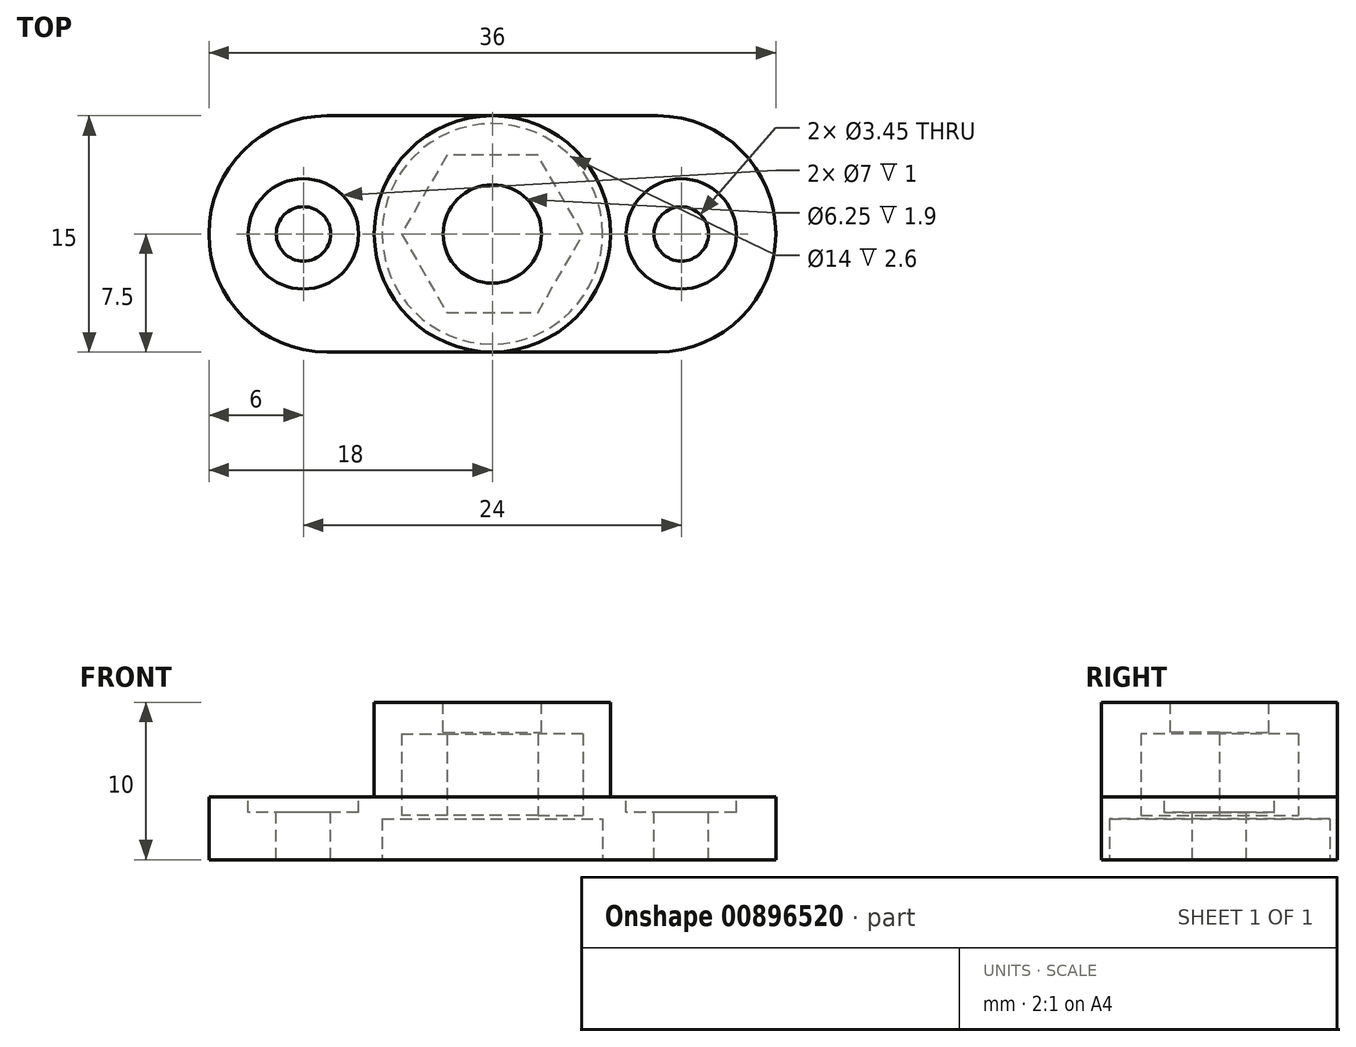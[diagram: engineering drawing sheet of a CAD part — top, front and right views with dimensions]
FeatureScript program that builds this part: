
annotation { "Feature Type Name" : "Feature", "Feature Type Description" : "" }
export const myFeature = defineFeature(function(context is Context, id is Id, definition is map)
    precondition{}
    {
        {
            var Q0;
            Q0=qCreatedBy(makeId("Top.planeOp"),FACE);
            var sketch = newSketch(context, id + "F0", { "sketchPlane" : qUnion([Q0])});
            skLineSegment(sketch, "E0.bottom", {"start": v(18, 7.5) * mm, "end": v(-18, 7.5) * mm});
            skLineSegment(sketch, "E0.top", {"start": v(18, -7.5) * mm, "end": v(-18, -7.5) * mm});
            skLineSegment(sketch, "E0.left", {"start": v(18, 7.5) * mm, "end": v(18, -7.5) * mm});
            skLineSegment(sketch, "E0.right", {"start": v(-18, 7.5) * mm, "end": v(-18, -7.5) * mm});
            skPoint(sketch, "E0.middle", {"position": v(0, 0) * mm});
            skSolve(sketch);
        }
        {
            var Q0;
            Q0 = qSketchRegion(id + "F0", true);
            extrude(context, id + "F1", {"entities" : qUnion([Q0]), "depth" : 4 * mm, "offsetDistance" : 25 * mm});
        }
        {
            var Q0;
            Q0=makeQuery(id+"F1.opExtrude","CAP_FACE",FACE,{"disambiguationData":[OSD([sQuery(id+"F0.wireOp",EDGE,"E0.bottom"),sQuery(id+"F0.wireOp",EDGE,"E0.top"),sQuery(id+"F0.wireOp",EDGE,"E0.left"),sQuery(id+"F0.wireOp",EDGE,"E0.right")])],"isStart":false});
            var sketch = newSketch(context, id + "F2", { "sketchPlane" : qUnion([Q0])});
            skCircle(sketch, "E1", {"center": v(0, 0) * mm, "radius": 7.5 * mm});
            skSolve(sketch);
        }
        {
            var Q0;
            Q0 = qSketchRegion(id + "F2", true);
            extrude(context, id + "F3", {"entities" : qUnion([Q0]), "operationType" : NewBodyOperationType.ADD, "depth" : 6 * mm, "offsetDistance" : 25 * mm});
        }
        {
            var Q0;
            Q0=makeQuery(id+"F1.opExtrude","SWEPT_EDGE",EDGE,{"disambiguationData":[OSD([sQuery(id+"F0.wireOp",EDGE,"E0.top"),sQuery(id+"F0.wireOp",EDGE,"E0.right")])]});
            var Q1;
            Q1=makeQuery(id+"F1.opExtrude","SWEPT_EDGE",EDGE,{"disambiguationData":[OSD([sQuery(id+"F0.wireOp",EDGE,"E0.bottom"),sQuery(id+"F0.wireOp",EDGE,"E0.right")])]});
            var Q2;
            Q2=makeQuery(id+"F1.opExtrude","SWEPT_EDGE",EDGE,{"disambiguationData":[OSD([sQuery(id+"F0.wireOp",EDGE,"E0.top"),sQuery(id+"F0.wireOp",EDGE,"E0.left")])]});
            var Q3;
            Q3=makeQuery(id+"F1.opExtrude","SWEPT_EDGE",EDGE,{"disambiguationData":[OSD([sQuery(id+"F0.wireOp",EDGE,"E0.bottom"),sQuery(id+"F0.wireOp",EDGE,"E0.left")])]});
            fillet(context, id + "F4", {"entities" : qUnion([Q0, Q1, Q2, Q3]), "radius" : 7.5 * mm, "tangentPropagation" : true, "allowEdgeOverflow" : false});
        }
        {
            var Q0;
            Q0=makeQuery(id+"F1.opExtrude","CAP_FACE",FACE,{"disambiguationData":[OSD([sQuery(id+"F0.wireOp",EDGE,"E0.bottom"),sQuery(id+"F0.wireOp",EDGE,"E0.top"),sQuery(id+"F0.wireOp",EDGE,"E0.left"),sQuery(id+"F0.wireOp",EDGE,"E0.right")])],"isStart":true});
            var sketch = newSketch(context, id + "F5", { "sketchPlane" : qUnion([Q0])});
            skCircle(sketch, "E2.cCircle", {"center": v(0, 0) * mm, "radius": 5 * mm, "construction": true});
            skLineSegment(sketch, "E2.0", {"start": v(-2.89, 5) * mm, "end": v(2.89, 5) * mm});
            skLineSegment(sketch, "E2.1", {"start": v(2.89, 5) * mm, "end": v(5.77, 0) * mm});
            skLineSegment(sketch, "E2.2", {"start": v(5.77, 0) * mm, "end": v(2.89, -5) * mm});
            skLineSegment(sketch, "E2.3", {"start": v(2.89, -5) * mm, "end": v(-2.89, -5) * mm});
            skLineSegment(sketch, "E2.4", {"start": v(-2.89, -5) * mm, "end": v(-5.77, 0) * mm});
            skLineSegment(sketch, "E2.5", {"start": v(-5.77, 0) * mm, "end": v(-2.89, 5) * mm});
            skPoint(sketch, "E2.0.midPoint", {"position": v(0, 5) * mm});
            skSolve(sketch);
        }
        {
            var Q0;
            Q0 = qSketchRegion(id + "F5", true);
            extrude(context, id + "F6", {"entities" : qUnion([Q0]), "operationType" : NewBodyOperationType.REMOVE, "oppositeDirection" : true, "depth" : 8 * mm, "offsetDistance" : 25 * mm});
        }
        {
            var Q0;
            {var subQ0=sQuery(id+"F0.wireOp",EDGE,"E0.top");var subQ1=sQuery(id+"F0.wireOp",EDGE,"E0.right");var subQ2=sQuery(id+"F0.wireOp",EDGE,"E0.bottom");var subQ3=makeQuery(id+"F1.opExtrude","CAP_FACE",FACE,{"disambiguationData":[OSD([subQ2,subQ0,sQuery(id+"F0.wireOp",EDGE,"E0.left"),subQ1])],"isStart":false});Q0=makeQuery(id+"F3.boolean.opBoolean","SPLIT",FACE,{"disambiguationData":[TD([makeQuery(id+"F1.opExtrude","SWEPT_FACE",FACE,{"disambiguationData":[OSD([subQ1])]})])],"derivedFrom":subQ3});}
            var sketch = newSketch(context, id + "F7", { "sketchPlane" : qUnion([Q0])});
            skCircle(sketch, "E3", {"center": v(-12, 0) * mm, "radius": 1.73 * mm});
            skCircle(sketch, "E4", {"center": v(12, 0) * mm, "radius": 1.73 * mm});
            skPoint(sketch, "E4.centerSnap0", {"position": v(-7.5, 0) * mm});
            skCircle(sketch, "E5", {"center": v(-12, 0) * mm, "radius": 3.5 * mm});
            skCircle(sketch, "E6", {"center": v(12, 0) * mm, "radius": 3.5 * mm});
            skSolve(sketch);
        }
        {
            var Q0;
            Q0=makeQuery(id+"F7.imprint","IMPRINT",FACE,{"disambiguationData":[TD([[makeQuery(id+"F7.imprint","IMPRINT",EDGE,{"derivedFrom":sQuery(id+"F7.wireOp",EDGE,"E4")}),1.0]])]});
            var Q1;
            Q1=makeQuery(id+"F7.imprint","IMPRINT",FACE,{"disambiguationData":[TD([[makeQuery(id+"F7.imprint","IMPRINT",EDGE,{"derivedFrom":sQuery(id+"F7.wireOp",EDGE,"E3")}),1.0]])]});
            extrude(context, id + "F8", {"entities" : qUnion([Q0, Q1]), "operationType" : NewBodyOperationType.REMOVE, "endBound" : BoundingType.UP_TO_NEXT, "oppositeDirection" : true, "depth" : 25 * mm, "offsetDistance" : 25 * mm});
        }
        {
            var Q0;
            Q0 = qSketchRegion(id + "F7", true);
            extrude(context, id + "F9", {"entities" : qUnion([Q0]), "operationType" : NewBodyOperationType.REMOVE, "oppositeDirection" : true, "depth" : 1 * mm, "offsetDistance" : 25 * mm});
        }
        {
            var Q0;
            Q0=makeQuery(id+"F3.opExtrude","CAP_FACE",FACE,{"disambiguationData":[OSD([sQuery(id+"F2.wireOp",EDGE,"E1")])],"isStart":false});
            var sketch = newSketch(context, id + "F10", { "sketchPlane" : qUnion([Q0])});
            skCircle(sketch, "E7", {"center": v(0, 0) * mm, "radius": 3.12 * mm});
            skSolve(sketch);
        }
        {
            var Q0;
            Q0 = qSketchRegion(id + "F10", true);
            extrude(context, id + "F11", {"entities" : qUnion([Q0]), "operationType" : NewBodyOperationType.REMOVE, "endBound" : BoundingType.UP_TO_NEXT, "oppositeDirection" : true, "depth" : 25 * mm, "offsetDistance" : 25 * mm});
        }
        {
            var Q0;
            Q0=makeQuery(id+"F6.boolean.opBoolean","COPY",FACE,{"derivedFrom":makeQuery(id+"F6.opExtrude","CAP_FACE",FACE,{"disambiguationData":[OSD([sQuery(id+"F5.wireOp",EDGE,"E2.0"),sQuery(id+"F5.wireOp",EDGE,"E2.1"),sQuery(id+"F5.wireOp",EDGE,"E2.2"),sQuery(id+"F5.wireOp",EDGE,"E2.3"),sQuery(id+"F5.wireOp",EDGE,"E2.4"),sQuery(id+"F5.wireOp",EDGE,"E2.5")])],"isStart":false})});
            var sketch = newSketch(context, id + "F12", { "sketchPlane" : qUnion([Q0])});
            skCircle(sketch, "E8", {"center": v(0, 0) * mm, "radius": 3.2 * mm});
            skSolve(sketch);
        }
        {
            var Q0;
            Q0 = qSketchRegion(id + "F12", true);
            extrude(context, id + "F13", {"entities" : qUnion([Q0]), "operationType" : NewBodyOperationType.ADD, "oppositeDirection" : true, "depth" : 0.1 * mm, "offsetDistance" : 25 * mm});
        }
        {
            var Q0;
            Q0=makeQuery(id+"F1.opExtrude","CAP_FACE",FACE,{"disambiguationData":[OSD([sQuery(id+"F0.wireOp",EDGE,"E0.bottom"),sQuery(id+"F0.wireOp",EDGE,"E0.top"),sQuery(id+"F0.wireOp",EDGE,"E0.left"),sQuery(id+"F0.wireOp",EDGE,"E0.right")])],"isStart":true});
            var sketch = newSketch(context, id + "F14", { "sketchPlane" : qUnion([Q0])});
            skCircle(sketch, "E9", {"center": v(0, 0) * mm, "radius": 7 * mm});
            skSolve(sketch);
        }
        {
            var Q0;
            Q0 = qSketchRegion(id + "F14", true);
            extrude(context, id + "F15", {"entities" : qUnion([Q0]), "operationType" : NewBodyOperationType.REMOVE, "oppositeDirection" : true, "depth" : (8 - (0.9 * 6)) * mm, "offsetDistance" : 25 * mm});
        }
        {
            var Q0;
            Q0=makeQuery(id+"F15.boolean.opBoolean","COPY",FACE,{"derivedFrom":makeQuery(id+"F15.opExtrude","CAP_FACE",FACE,{"disambiguationData":[OSD([sQuery(id+"F14.wireOp",EDGE,"E9")])],"isStart":false})});
            var sketch = newSketch(context, id + "F16", { "sketchPlane" : qUnion([Q0])});
            skCircle(sketch, "E10.cCircle", {"center": v(0, 0) * mm, "radius": 5 * mm, "construction": true});
            skLineSegment(sketch, "E10.0", {"start": v(-2.89, 5) * mm, "end": v(2.89, 5) * mm});
            skLineSegment(sketch, "E10.1", {"start": v(2.89, 5) * mm, "end": v(5.77, 0) * mm});
            skLineSegment(sketch, "E10.2", {"start": v(5.77, 0) * mm, "end": v(2.89, -5) * mm});
            skLineSegment(sketch, "E10.3", {"start": v(2.89, -5) * mm, "end": v(-2.89, -5) * mm});
            skLineSegment(sketch, "E10.4", {"start": v(-2.89, -5) * mm, "end": v(-5.77, 0) * mm});
            skLineSegment(sketch, "E10.5", {"start": v(-5.77, 0) * mm, "end": v(-2.89, 5) * mm});
            skPoint(sketch, "E10.0.midPoint", {"position": v(0, 5) * mm});
            skSolve(sketch);
        }
        {
            var Q0;
            Q0 = qSketchRegion(id + "F16", true);
            extrude(context, id + "F17", {"entities" : qUnion([Q0]), "operationType" : NewBodyOperationType.ADD, "oppositeDirection" : true, "depth" : 0.2 * mm, "offsetDistance" : 25 * mm});
        }
    });
